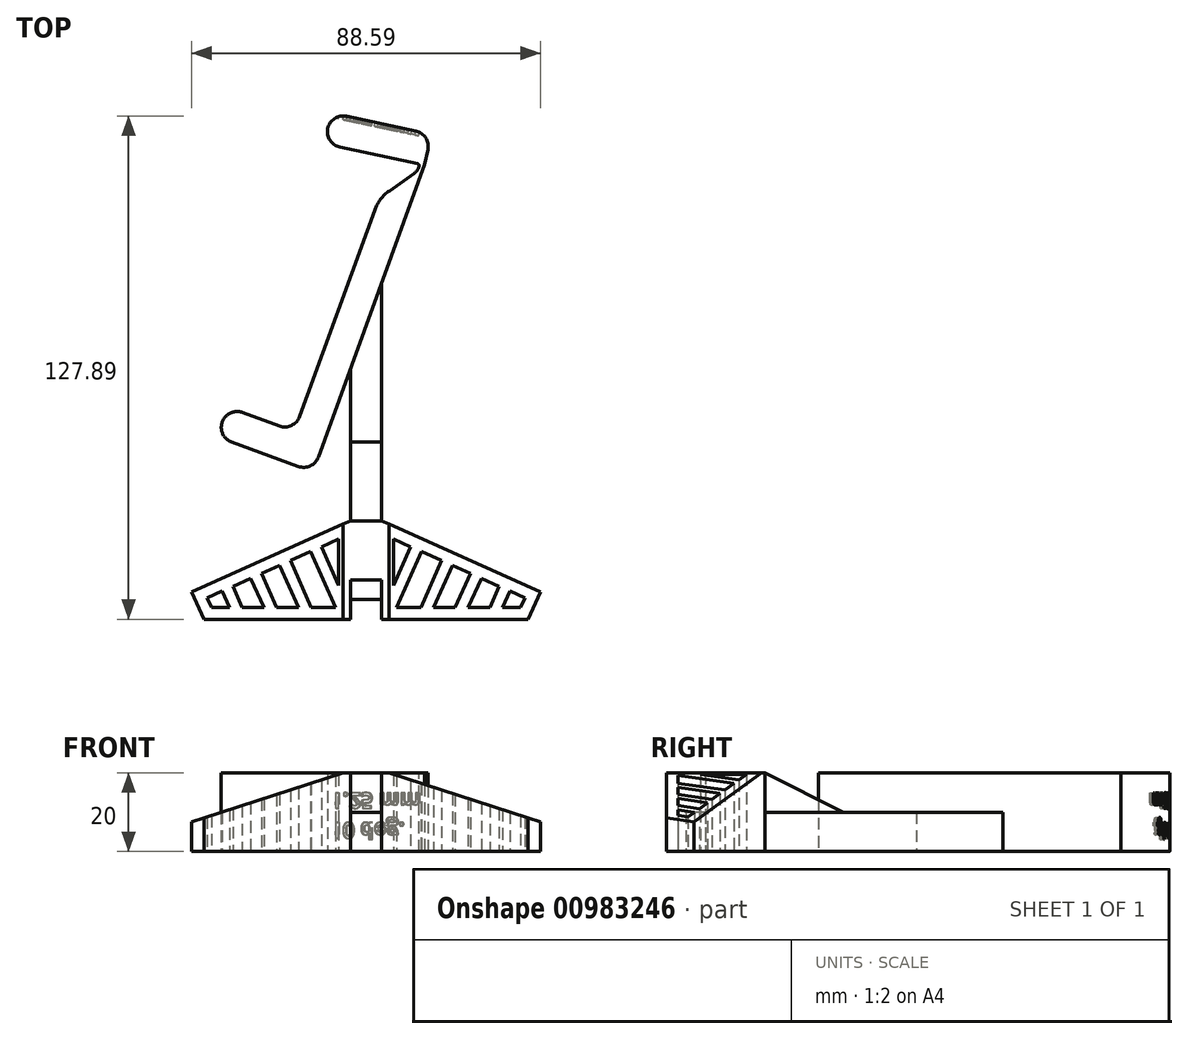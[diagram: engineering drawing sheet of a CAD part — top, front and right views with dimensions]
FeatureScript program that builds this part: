
annotation { "Feature Type Name" : "Feature", "Feature Type Description" : "" }
export const myFeature = defineFeature(function(context is Context, id is Id, definition is map)
    precondition{}
    {
        {
            var Q0;
            Q0=qCreatedBy(makeId("Top.planeOp"),FACE);
            var sketch = newSketch(context, id + "F0", { "sketchPlane" : qUnion([Q0])});
            skLineSegment(sketch, "E0", {"start": v(-17.1, -7) * mm, "end": v(8.55, 63.48) * mm});
            skLineSegment(sketch, "E1", {"start": v(-17.1, -7) * mm, "end": v(-34.02, -0.84) * mm});
            skLineSegment(sketch, "E2", {"start": v(-34.02, -0.84) * mm, "end": v(-36.75, -8.36) * mm});
            skLineSegment(sketch, "E3", {"start": v(-36.75, -8.36) * mm, "end": v(-12.32, -17.25) * mm});
            skLineSegment(sketch, "E4", {"start": v(-12.32, -17.25) * mm, "end": v(16.07, 60.74) * mm});
            skLineSegment(sketch, "E5", {"start": v(17.69, 68.48) * mm, "end": v(-22.23, 83.01) * mm});
            skLineSegment(sketch, "E6", {"start": v(17.69, 68.48) * mm, "end": v(-7.75, 73.89) * mm});
            skLineSegment(sketch, "E7", {"start": v(-7.75, 73.89) * mm, "end": v(-9.4, 66.06) * mm});
            skLineSegment(sketch, "E8", {"start": v(-9.4, 66.06) * mm, "end": v(14.8, 60.92) * mm});
            skLineSegment(sketch, "E9", {"start": v(14.8, 60.92) * mm, "end": v(14.12, 59.04) * mm});
            skLineSegment(sketch, "E10", {"start": v(14.12, 59.04) * mm, "end": v(4.48, 52.29) * mm});
            skLineSegment(sketch, "E11", {"start": v(16.07, 60.74) * mm, "end": v(17.69, 68.48) * mm});
            skLineSegment(sketch, "E12", {"start": v(-2.85, 8.76) * mm, "end": v(-2.85, -29.75) * mm});
            skLineSegment(sketch, "E13", {"start": v(-2.85, -29.75) * mm, "end": v(-43.15, -47.75) * mm});
            skLineSegment(sketch, "E14", {"start": v(-43.15, -47.75) * mm, "end": v(-40.02, -54.75) * mm});
            skLineSegment(sketch, "E15", {"start": v(-40.02, -54.75) * mm, "end": v(-2.85, -54.75) * mm});
            skLineSegment(sketch, "E16", {"start": v(-2.85, -54.75) * mm, "end": v(-2.85, -29.75) * mm});
            skLineSegment(sketch, "E17", {"start": v(5.15, 30.74) * mm, "end": v(5.15, -54.75) * mm});
            skLineSegment(sketch, "E18", {"start": v(-2.85, -54.75) * mm, "end": v(5.15, -54.75) * mm});
            skLineSegment(sketch, "E19", {"start": v(5.15, -29.75) * mm, "end": v(-2.85, -29.75) * mm});
            skLineSegment(sketch, "E20.MirrorCS", {"start": v(5.15, -29.75) * mm, "end": v(45.44, -47.75) * mm});
            skLineSegment(sketch, "E21.MirrorCS", {"start": v(45.44, -47.75) * mm, "end": v(42.3, -54.75) * mm});
            skLineSegment(sketch, "E22.MirrorCS", {"start": v(42.3, -54.75) * mm, "end": v(5.15, -54.75) * mm});
            skLineSegment(sketch, "E23.MirrorCS", {"start": v(5.15, -54.75) * mm, "end": v(5.15, -29.75) * mm});
            skLineSegment(sketch, "E24", {"start": v(-2.85, -49.75) * mm, "end": v(5.15, -49.75) * mm});
            skLineSegment(sketch, "E25", {"start": v(-2.85, -44.75) * mm, "end": v(5.15, -44.75) * mm});
            skLineSegment(sketch, "E26.0", {"start": v(-5.85, -34.38) * mm, "end": v(-44.74, -51.75) * mm});
            skLineSegment(sketch, "E26.1", {"start": v(-5.85, -51.75) * mm, "end": v(-5.85, -34.38) * mm});
            skLineSegment(sketch, "E26.2", {"start": v(-44.74, -51.75) * mm, "end": v(-5.85, -51.75) * mm});
            skLineSegment(sketch, "E27", {"start": v(-28.13, -44.33) * mm, "end": v(-24.82, -51.75) * mm});
            skLineSegment(sketch, "E28", {"start": v(-25.4, -43.1) * mm, "end": v(-21.53, -51.75) * mm});
            skLineSegment(sketch, "E29", {"start": v(-20.83, -41.07) * mm, "end": v(-16.05, -51.75) * mm});
            skLineSegment(sketch, "E30", {"start": v(-18.09, -39.84) * mm, "end": v(-12.77, -51.75) * mm});
            skLineSegment(sketch, "E31", {"start": v(-12.95, -37.55) * mm, "end": v(-6.6, -51.75) * mm});
            skLineSegment(sketch, "E32", {"start": v(-10.21, -36.33) * mm, "end": v(-5.85, -46.08) * mm});
            skPoint(sketch, "E33", {"position": v(1.15, -44.75) * mm});
            skLineSegment(sketch, "E34", {"start": v(1.15, -44.75) * mm, "end": v(1.15, -20.25) * mm});
            skLineSegment(sketch, "E35", {"start": v(-39.18, -49.27) * mm, "end": v(-38.07, -51.75) * mm});
            skLineSegment(sketch, "E36", {"start": v(-35.44, -47.6) * mm, "end": v(-33.58, -51.75) * mm});
            skLineSegment(sketch, "E37", {"start": v(-32.7, -46.37) * mm, "end": v(-30.3, -51.75) * mm});
            skLineSegment(sketch, "E38.MirrorCS", {"start": v(37.73, -47.6) * mm, "end": v(35.87, -51.75) * mm});
            skLineSegment(sketch, "E39.MirrorCS", {"start": v(20.38, -39.84) * mm, "end": v(15.06, -51.75) * mm});
            skLineSegment(sketch, "E40.MirrorCS", {"start": v(15.24, -37.55) * mm, "end": v(8.9, -51.75) * mm});
            skLineSegment(sketch, "E41.MirrorCS", {"start": v(8.15, -51.75) * mm, "end": v(8.15, -34.38) * mm});
            skLineSegment(sketch, "E42.MirrorCS", {"start": v(8.15, -34.38) * mm, "end": v(47.04, -51.75) * mm});
            skLineSegment(sketch, "E43.MirrorCS", {"start": v(23.12, -41.07) * mm, "end": v(18.35, -51.75) * mm});
            skLineSegment(sketch, "E44.MirrorCS", {"start": v(12.5, -36.33) * mm, "end": v(8.15, -46.08) * mm});
            skLineSegment(sketch, "E45.MirrorCS", {"start": v(47.04, -51.75) * mm, "end": v(8.15, -51.75) * mm});
            skLineSegment(sketch, "E46.MirrorCS", {"start": v(34.99, -46.37) * mm, "end": v(32.58, -51.75) * mm});
            skLineSegment(sketch, "E47.MirrorCS", {"start": v(30.42, -44.33) * mm, "end": v(27.1, -51.75) * mm});
            skLineSegment(sketch, "E48.MirrorCS", {"start": v(41.47, -49.27) * mm, "end": v(40.36, -51.75) * mm});
            skLineSegment(sketch, "E49.MirrorCS", {"start": v(27.68, -43.1) * mm, "end": v(23.82, -51.75) * mm});
            skLineSegment(sketch, "E50", {"start": v(-43.15, -47.75) * mm, "end": v(-43.15, -54.75) * mm});
            skLineSegment(sketch, "E51", {"start": v(-43.15, -54.75) * mm, "end": v(-40.02, -54.75) * mm});
            skLineSegment(sketch, "E52", {"start": v(45.44, -47.75) * mm, "end": v(45.44, -54.75) * mm});
            skLineSegment(sketch, "E53", {"start": v(45.44, -54.75) * mm, "end": v(42.3, -54.75) * mm});
            skSolve(sketch);
        }
        {
            var Q0;
            {var subQ9=sQuery(id+"F0.wireOp",EDGE,"E1");Q0=makeQuery(id+"F0.imprint","IMPRINT",FACE,{"disambiguationData":[TD([[makeQuery(id+"F0.imprint","IMPRINT",EDGE,{"derivedFrom":subQ9}),1.0]])]});}
            var Q1;
            {var subQ1=sQuery(id+"F0.wireOp",EDGE,"E16");var subQ3=sQuery(id+"F0.wireOp",EDGE,"E25");var subQ4=makeQuery(id+"F0.imprint","INTERSECT",VERTEX,{"derivedFrom":[subQ1,subQ3]});Q1=makeQuery(id+"F0.imprint","IMPRINT",FACE,{"disambiguationData":[TD([[makeQuery(id+"F0.imprint","IMPRINT",EDGE,{"disambiguationData":[TD([[subQ4,-1.0]])],"derivedFrom":subQ3}),1.0]])]});}
            var Q2;
            {var subQ1=sQuery(id+"F0.wireOp",EDGE,"E17");var subQ3=sQuery(id+"F0.wireOp",EDGE,"E25");var subQ4=makeQuery(id+"F0.imprint","INTERSECT",VERTEX,{"derivedFrom":[subQ1,subQ3]});Q2=makeQuery(id+"F0.imprint","IMPRINT",FACE,{"disambiguationData":[TD([[makeQuery(id+"F0.imprint","IMPRINT",EDGE,{"disambiguationData":[TD([[subQ4,1.0]])],"derivedFrom":subQ3}),1.0]])]});}
            var Q3;
            {var subQ32=sQuery(id+"F0.wireOp",EDGE,"E13");Q3=makeQuery(id+"F0.imprint","IMPRINT",FACE,{"disambiguationData":[TD([[makeQuery(id+"F0.imprint","IMPRINT",EDGE,{"derivedFrom":subQ32}),1.0]])]});}
            var Q4;
            {var subQ0=sQuery(id+"F0.wireOp",EDGE,"E31");Q4=makeQuery(id+"F0.imprint","IMPRINT",FACE,{"disambiguationData":[TD([[makeQuery(id+"F0.imprint","IMPRINT",EDGE,{"derivedFrom":subQ0}),1.0]])]});}
            var Q5;
            {var subQ0=sQuery(id+"F0.wireOp",EDGE,"E29");Q5=makeQuery(id+"F0.imprint","IMPRINT",FACE,{"disambiguationData":[TD([[makeQuery(id+"F0.imprint","IMPRINT",EDGE,{"derivedFrom":subQ0}),1.0]])]});}
            var Q6;
            {var subQ0=sQuery(id+"F0.wireOp",EDGE,"E27");Q6=makeQuery(id+"F0.imprint","IMPRINT",FACE,{"disambiguationData":[TD([[makeQuery(id+"F0.imprint","IMPRINT",EDGE,{"derivedFrom":subQ0}),1.0]])]});}
            var Q7;
            {var subQ0=sQuery(id+"F0.wireOp",EDGE,"E36");Q7=makeQuery(id+"F0.imprint","IMPRINT",FACE,{"disambiguationData":[TD([[makeQuery(id+"F0.imprint","IMPRINT",EDGE,{"derivedFrom":subQ0}),1.0]])]});}
            var Q8;
            {var subQ5=sQuery(id+"F0.wireOp",EDGE,"E35");Q8=makeQuery(id+"F0.imprint","IMPRINT",FACE,{"disambiguationData":[TD([[makeQuery(id+"F0.imprint","IMPRINT",EDGE,{"derivedFrom":subQ5}),-1.0]])]});}
            var Q9;
            {var subQ3=sQuery(id+"F0.wireOp",EDGE,"E51");Q9=makeQuery(id+"F0.imprint","IMPRINT",FACE,{"disambiguationData":[TD([[makeQuery(id+"F0.imprint","IMPRINT",EDGE,{"derivedFrom":subQ3}),1.0]])]});}
            var Q10;
            {var subQ0=sQuery(id+"F0.wireOp",EDGE,"E26.2");var subQ1=sQuery(id+"F0.wireOp",EDGE,"E14");var subQ2=makeQuery(id+"F0.imprint","INTERSECT",VERTEX,{"derivedFrom":[subQ1,subQ0]});Q10=makeQuery(id+"F0.imprint","IMPRINT",FACE,{"disambiguationData":[TD([[makeQuery(id+"F0.imprint","IMPRINT",EDGE,{"disambiguationData":[TD([[subQ2,1.0]])],"derivedFrom":subQ1}),-1.0]])]});}
            var Q11;
            {var subQ0=sQuery(id+"F0.wireOp",EDGE,"E50");var subQ3=sQuery(id+"F0.wireOp",EDGE,"E26.0");var subQ5=makeQuery(id+"F0.imprint","INTERSECT",VERTEX,{"derivedFrom":[subQ3,subQ0]});Q11=makeQuery(id+"F0.imprint","IMPRINT",FACE,{"disambiguationData":[TD([[makeQuery(id+"F0.imprint","IMPRINT",EDGE,{"disambiguationData":[TD([[subQ5,1.0]])],"derivedFrom":subQ3}),-1.0]])]});}
            var Q12;
            {var subQ3=sQuery(id+"F0.wireOp",EDGE,"E53");Q12=makeQuery(id+"F0.imprint","IMPRINT",FACE,{"disambiguationData":[TD([[makeQuery(id+"F0.imprint","IMPRINT",EDGE,{"derivedFrom":subQ3}),-1.0]])]});}
            var Q13;
            {var subQ0=sQuery(id+"F0.wireOp",EDGE,"E45.MirrorCS");var subQ1=sQuery(id+"F0.wireOp",EDGE,"E21.MirrorCS");var subQ2=makeQuery(id+"F0.imprint","INTERSECT",VERTEX,{"derivedFrom":[subQ1,subQ0]});Q13=makeQuery(id+"F0.imprint","IMPRINT",FACE,{"disambiguationData":[TD([[makeQuery(id+"F0.imprint","IMPRINT",EDGE,{"disambiguationData":[TD([[subQ2,1.0]])],"derivedFrom":subQ1}),1.0]])]});}
            var Q14;
            {var subQ0=sQuery(id+"F0.wireOp",EDGE,"E52");var subQ3=sQuery(id+"F0.wireOp",EDGE,"E42.MirrorCS");var subQ5=makeQuery(id+"F0.imprint","INTERSECT",VERTEX,{"derivedFrom":[subQ3,subQ0]});Q14=makeQuery(id+"F0.imprint","IMPRINT",FACE,{"disambiguationData":[TD([[makeQuery(id+"F0.imprint","IMPRINT",EDGE,{"disambiguationData":[TD([[subQ5,1.0]])],"derivedFrom":subQ3}),1.0]])]});}
            var Q15;
            {var subQ27=sQuery(id+"F0.wireOp",EDGE,"E20.MirrorCS");Q15=makeQuery(id+"F0.imprint","IMPRINT",FACE,{"disambiguationData":[TD([[makeQuery(id+"F0.imprint","IMPRINT",EDGE,{"derivedFrom":subQ27}),-1.0]])]});}
            var Q16;
            {var subQ5=sQuery(id+"F0.wireOp",EDGE,"E48.MirrorCS");Q16=makeQuery(id+"F0.imprint","IMPRINT",FACE,{"disambiguationData":[TD([[makeQuery(id+"F0.imprint","IMPRINT",EDGE,{"derivedFrom":subQ5}),1.0]])]});}
            var Q17;
            {var subQ0=sQuery(id+"F0.wireOp",EDGE,"E38.MirrorCS");Q17=makeQuery(id+"F0.imprint","IMPRINT",FACE,{"disambiguationData":[TD([[makeQuery(id+"F0.imprint","IMPRINT",EDGE,{"derivedFrom":subQ0}),-1.0]])]});}
            var Q18;
            {var subQ0=sQuery(id+"F0.wireOp",EDGE,"E47.MirrorCS");Q18=makeQuery(id+"F0.imprint","IMPRINT",FACE,{"disambiguationData":[TD([[makeQuery(id+"F0.imprint","IMPRINT",EDGE,{"derivedFrom":subQ0}),-1.0]])]});}
            var Q19;
            {var subQ0=sQuery(id+"F0.wireOp",EDGE,"E39.MirrorCS");Q19=makeQuery(id+"F0.imprint","IMPRINT",FACE,{"disambiguationData":[TD([[makeQuery(id+"F0.imprint","IMPRINT",EDGE,{"derivedFrom":subQ0}),1.0]])]});}
            var Q20;
            {var subQ2=sQuery(id+"F0.wireOp",EDGE,"E40.MirrorCS");Q20=makeQuery(id+"F0.imprint","IMPRINT",FACE,{"disambiguationData":[TD([[makeQuery(id+"F0.imprint","IMPRINT",EDGE,{"derivedFrom":subQ2}),-1.0]])]});}
            extrude(context, id + "F1", {"entities" : qUnion([Q0, Q1, Q2, Q3, Q4, Q5, Q6, Q7, Q8, Q9, Q10, Q11, Q12, Q13, Q14, Q15, Q16, Q17, Q18, Q19, Q20]), "depth" : 20 * mm, "offsetDistance" : 25 * mm});
        }
        {
            var Q0;
            Q0=makeQuery(id+"F1.opExtrude","SWEPT_FACE",FACE,{"disambiguationData":[OSD([sQuery(id+"F0.wireOp",EDGE,"E6")])]});
            var sketch = newSketch(context, id + "F2", { "sketchPlane" : qUnion([Q0])});
            skText(sketch, "E54", { "text": "10 deg.\n1.25 mm", "fontName": "OpenSans-Bold.ttf"});
            const initialGuessF2  = {"E54": [0.02302, 0.00736, -1, 0, 0.004]};
            skSetInitialGuess(sketch, initialGuessF2);
            skSolve(sketch);
        }
        {
            var Q0;
            Q0=qSketchRegion(id+"F2",true);
            extrude(context, id + "F3", {"entities" : qUnion([Q0]), "operationType" : NewBodyOperationType.REMOVE, "oppositeDirection" : true, "depth" : 1 * mm, "offsetDistance" : 25 * mm});
        }
        {
            var Q0;
            Q0=makeQuery(id+"F1.opExtrude","SWEPT_EDGE",EDGE,{"disambiguationData":[OSD([sQuery(id+"F0.wireOp",EDGE,"E1"),sQuery(id+"F0.wireOp",EDGE,"E2")])]});
            var Q1;
            Q1=makeQuery(id+"F1.opExtrude","SWEPT_EDGE",EDGE,{"disambiguationData":[OSD([sQuery(id+"F0.wireOp",EDGE,"E2"),sQuery(id+"F0.wireOp",EDGE,"E3")])]});
            var Q2;
            Q2=makeQuery(id+"F1.opExtrude","SWEPT_EDGE",EDGE,{"disambiguationData":[OSD([sQuery(id+"F0.wireOp",EDGE,"E0"),sQuery(id+"F0.wireOp",EDGE,"E1")])]});
            var Q3;
            Q3=makeQuery(id+"F1.opExtrude","SWEPT_EDGE",EDGE,{"disambiguationData":[OSD([sQuery(id+"F0.wireOp",EDGE,"E3"),sQuery(id+"F0.wireOp",EDGE,"E4")])]});
            fillet(context, id + "F4", {"entities" : qUnion([Q0, Q1, Q2, Q3]), "radius" : 4 * mm, "tangentPropagation" : true, "allowEdgeOverflow" : false});
        }
        {
            var Q0;
            Q0=makeQuery(id+"F1.opExtrude","SWEPT_EDGE",EDGE,{"disambiguationData":[OSD([sQuery(id+"F0.wireOp",EDGE,"E0"),sQuery(id+"F0.wireOp",EDGE,"E10")])]});
            fillet(context, id + "F5", {"entities" : qUnion([Q0]), "radius" : 10 * mm, "tangentPropagation" : true, "allowEdgeOverflow" : false});
        }
        {
            var Q0;
            Q0=makeQuery(id+"F1.opExtrude","SWEPT_EDGE",EDGE,{"disambiguationData":[OSD([sQuery(id+"F0.wireOp",EDGE,"E8"),sQuery(id+"F0.wireOp",EDGE,"E9")])]});
            fillet(context, id + "F6", {"entities" : qUnion([Q0]), "radius" : 0.5 * mm, "tangentPropagation" : true, "allowEdgeOverflow" : false});
        }
        {
            var Q0;
            Q0=makeQuery(id+"F1.opExtrude","SWEPT_EDGE",EDGE,{"disambiguationData":[OSD([sQuery(id+"F0.wireOp",EDGE,"E9"),sQuery(id+"F0.wireOp",EDGE,"E10")])]});
            fillet(context, id + "F7", {"entities" : qUnion([Q0]), "radius" : 3 * mm, "tangentPropagation" : true, "allowEdgeOverflow" : false});
        }
        {
            var Q0;
            Q0=makeQuery(id+"F1.opExtrude","SWEPT_EDGE",EDGE,{"disambiguationData":[OSD([sQuery(id+"F0.wireOp",EDGE,"E7"),sQuery(id+"F0.wireOp",EDGE,"E8")])]});
            var Q1;
            Q1=makeQuery(id+"F1.opExtrude","SWEPT_EDGE",EDGE,{"disambiguationData":[OSD([sQuery(id+"F0.wireOp",EDGE,"E6"),sQuery(id+"F0.wireOp",EDGE,"E7")])]});
            var Q2;
            Q2=makeQuery(id+"F1.opExtrude","SWEPT_EDGE",EDGE,{"disambiguationData":[OSD([sQuery(id+"F0.wireOp",EDGE,"E6"),sQuery(id+"F0.wireOp",EDGE,"E11")])]});
            fillet(context, id + "F8", {"entities" : qUnion([Q0, Q1, Q2]), "radius" : 4 * mm, "tangentPropagation" : true, "allowEdgeOverflow" : false});
        }
        {
            var Q0;
            {var subQ1=sQuery(id+"F0.wireOp",EDGE,"E12");Q0=makeQuery(id+"F0.imprint","IMPRINT",FACE,{"disambiguationData":[TD([[makeQuery(id+"F0.imprint","IMPRINT",EDGE,{"derivedFrom":subQ1}),1.0]])]});}
            var Q1;
            {var subQ4=sQuery(id+"F0.wireOp",EDGE,"E24");Q1=makeQuery(id+"F0.imprint","IMPRINT",FACE,{"disambiguationData":[TD([[makeQuery(id+"F0.imprint","IMPRINT",EDGE,{"derivedFrom":subQ4}),1.0]])]});}
            extrude(context, id + "F9", {"entities" : qUnion([Q0, Q1]), "depth" : 10 * mm, "offsetDistance" : 25 * mm});
        }
        {
            var Q0;
            Q0=makeQuery(id+"F1.opExtrude","CAP_EDGE",EDGE,{"disambiguationData":[OSD([sQuery(id+"F0.wireOp",EDGE,"E50")])],"isStart":false});
            chamfer(context, id + "F10", {"entities" : qUnion([Q0]), "chamferType" : ChamferType.OFFSET_ANGLE, "width" : 12.5 * mm, "oppositeDirection" : true, "angle" : 72 * degree, "tangentPropagation" : true});
        }
        {
            var Q0;
            Q0=makeQuery(id+"F1.opExtrude","CAP_EDGE",EDGE,{"disambiguationData":[OSD([sQuery(id+"F0.wireOp",EDGE,"E52")])],"isStart":false});
            chamfer(context, id + "F11", {"entities" : qUnion([Q0]), "chamferType" : ChamferType.OFFSET_ANGLE, "width" : 12.5 * mm, "oppositeDirection" : false, "angle" : 72 * degree, "tangentPropagation" : true});
        }
        {
            var Q0;
            {var subQ0=sQuery(id+"F0.wireOp",EDGE,"E50");var subQ3=sQuery(id+"F0.wireOp",EDGE,"E26.0");var subQ5=makeQuery(id+"F0.imprint","INTERSECT",VERTEX,{"derivedFrom":[subQ3,subQ0]});Q0=makeQuery(id+"F0.imprint","IMPRINT",FACE,{"disambiguationData":[TD([[makeQuery(id+"F0.imprint","IMPRINT",EDGE,{"disambiguationData":[TD([[subQ5,1.0]])],"derivedFrom":subQ3}),-1.0]])]});}
            var Q1;
            {var subQ0=sQuery(id+"F0.wireOp",EDGE,"E26.2");var subQ1=sQuery(id+"F0.wireOp",EDGE,"E14");var subQ2=makeQuery(id+"F0.imprint","INTERSECT",VERTEX,{"derivedFrom":[subQ1,subQ0]});Q1=makeQuery(id+"F0.imprint","IMPRINT",FACE,{"disambiguationData":[TD([[makeQuery(id+"F0.imprint","IMPRINT",EDGE,{"disambiguationData":[TD([[subQ2,1.0]])],"derivedFrom":subQ1}),-1.0]])]});}
            var Q2;
            {var subQ3=sQuery(id+"F0.wireOp",EDGE,"E51");Q2=makeQuery(id+"F0.imprint","IMPRINT",FACE,{"disambiguationData":[TD([[makeQuery(id+"F0.imprint","IMPRINT",EDGE,{"derivedFrom":subQ3}),1.0]])]});}
            var Q3;
            {var subQ3=sQuery(id+"F0.wireOp",EDGE,"E53");Q3=makeQuery(id+"F0.imprint","IMPRINT",FACE,{"disambiguationData":[TD([[makeQuery(id+"F0.imprint","IMPRINT",EDGE,{"derivedFrom":subQ3}),-1.0]])]});}
            var Q4;
            {var subQ0=sQuery(id+"F0.wireOp",EDGE,"E45.MirrorCS");var subQ1=sQuery(id+"F0.wireOp",EDGE,"E21.MirrorCS");var subQ2=makeQuery(id+"F0.imprint","INTERSECT",VERTEX,{"derivedFrom":[subQ1,subQ0]});Q4=makeQuery(id+"F0.imprint","IMPRINT",FACE,{"disambiguationData":[TD([[makeQuery(id+"F0.imprint","IMPRINT",EDGE,{"disambiguationData":[TD([[subQ2,1.0]])],"derivedFrom":subQ1}),1.0]])]});}
            var Q5;
            {var subQ0=sQuery(id+"F0.wireOp",EDGE,"E52");var subQ3=sQuery(id+"F0.wireOp",EDGE,"E42.MirrorCS");var subQ5=makeQuery(id+"F0.imprint","INTERSECT",VERTEX,{"derivedFrom":[subQ3,subQ0]});Q5=makeQuery(id+"F0.imprint","IMPRINT",FACE,{"disambiguationData":[TD([[makeQuery(id+"F0.imprint","IMPRINT",EDGE,{"disambiguationData":[TD([[subQ5,1.0]])],"derivedFrom":subQ3}),1.0]])]});}
            extrude(context, id + "F12", {"entities" : qUnion([Q0, Q1, Q2, Q3, Q4, Q5]), "operationType" : NewBodyOperationType.REMOVE, "depth" : 10 * mm, "offsetDistance" : 25 * mm});
        }
        {
            var Q0;
            {var subQ0=sQuery(id+"F0.wireOp",EDGE,"E17");Q0=makeQuery(id+"F9.opExtrude","SWEPT_FACE",FACE,{"disambiguationData":[OSD([subQ0]),TDD([makeQuery(id+"F0.imprint","IMPRINT",EDGE,{"disambiguationData":[TD([[makeQuery(id+"F0.imprint","INTERSECT",VERTEX,{"derivedFrom":[sQuery(id+"F0.wireOp",EDGE,"E4"),subQ0]}),-1.0]])],"derivedFrom":subQ0})])]});}
            var sketch = newSketch(context, id + "F13", { "sketchPlane" : qUnion([Q0])});
            skLineSegment(sketch, "E55", {"start": v(-29.75, 10) * mm, "end": v(-29.75, 20) * mm});
            skLineSegment(sketch, "E56", {"start": v(-29.75, 20) * mm, "end": v(-9.75, 10) * mm});
            skLineSegment(sketch, "E57", {"start": v(-9.75, 10) * mm, "end": v(-29.75, 10) * mm});
            skSolve(sketch);
        }
        {
            var Q0;
            Q0=makeQuery(id+"F13.imprint","IMPRINT",FACE,{"disambiguationData":[TD([[makeQuery(id+"F13.imprint","IMPRINT",EDGE,{"derivedFrom":sQuery(id+"F13.wireOp",EDGE,"E55")}),-1.0]])]});
            extrude(context, id + "F14", {"entities" : qUnion([Q0]), "oppositeDirection" : true, "depth" : 8 * mm, "offsetDistance" : 25 * mm});
        }
    });
